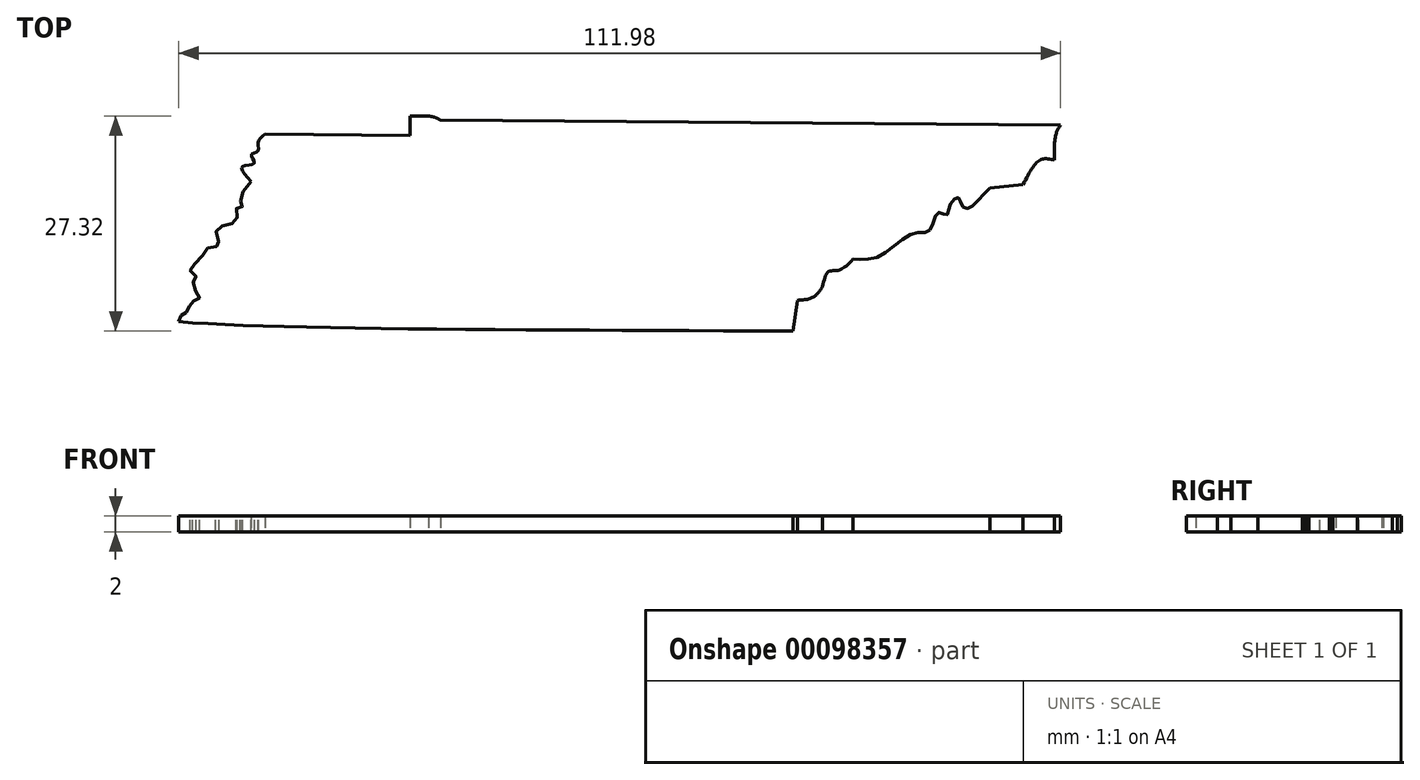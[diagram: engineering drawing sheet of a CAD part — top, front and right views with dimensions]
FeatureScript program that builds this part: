
annotation { "Feature Type Name" : "Feature", "Feature Type Description" : "" }
export const myFeature = defineFeature(function(context is Context, id is Id, definition is map)
    precondition{}
    {
        {
            var Q0;
            Q0=qCreatedBy(makeId("Top.planeOp"),FACE);
            var sketch = newSketch(context, id + "F0", { "sketchPlane" : qUnion([Q0])});
            skLineSegment(sketch, "E0", {"start": v(-26.82, 16.94) * mm, "end": v(51.93, 16.28) * mm});
            skFitSpline(sketch, "E1", {"points": [v(51.93, 16.28) * mm, v(51.35, 15.08) * mm, v(51.16, 11.87) * mm], "startDerivative": vector(-1.7, -2.63) * mm, "endDerivative": vector(0.03, -5.95) * mm});
            skFitSpline(sketch, "E2", {"points": [v(51.16, 11.87) * mm, v(49.38, 11.87) * mm, v(47.2, 8.76) * mm], "startDerivative": vector(-4.52, 1.06) * mm, "endDerivative": vector(-3.45, -6.8) * mm});
            skLineSegment(sketch, "E3", {"start": v(47.2, 8.76) * mm, "end": v(43, 8.31) * mm});
            skLineSegment(sketch, "E4", {"start": v(43, 8.31) * mm, "end": v(40.78, 6.04) * mm});
            skFitSpline(sketch, "E5", {"points": [v(40.78, 6.04) * mm, v(39.58, 5.91) * mm, v(38.96, 7.09) * mm, v(37.87, 6.12) * mm, v(37.5, 4.88) * mm, v(36.39, 5.2) * mm, v(35.38, 2.97) * mm, v(33.23, 2.56) * mm, v(28.92, -0.36) * mm, v(25.6, -0.72) * mm], "startDerivative": vector(-13.2, -13.48) * mm, "endDerivative": vector(-18.35, 0.4) * mm});
            skFitSpline(sketch, "E6", {"points": [v(25.6, -0.72) * mm, v(23.75, -2.13) * mm, v(22.51, -2.31) * mm, v(21.72, -4.21) * mm], "startDerivative": vector(-4.68, -5.49) * mm, "endDerivative": vector(-1.48, -7.24) * mm});
            skFitSpline(sketch, "E7", {"points": [v(21.72, -4.21) * mm, v(20.54, -5.55) * mm, v(18.51, -5.95) * mm], "startDerivative": vector(-2.1, -3.26) * mm, "endDerivative": vector(-4.29, -0.18) * mm});
            skLineSegment(sketch, "E8", {"start": v(18.51, -5.95) * mm, "end": v(17.98, -9.87) * mm});
            skFitSpline(sketch, "E9", {"points": [v(17.98, -9.87) * mm, v(-60.05, -8.68) * mm], "startDerivative": vector(-102.57, 0.48) * mm, "endDerivative": vector(-37.82, 3.1) * mm});
            skFitSpline(sketch, "E10", {"points": [v(-60.05, -8.68) * mm, v(-59.73, -7.88) * mm, v(-59.16, -7.52) * mm, v(-58.58, -6.56) * mm, v(-58.02, -5.94) * mm, v(-57.39, -5.57) * mm, v(-58.3, -3.97) * mm, v(-57.83, -3.01) * mm, v(-58.63, -2.14) * mm, v(-57.35, -0.68) * mm, v(-56.26, 0.73) * mm, v(-54.97, 1.01) * mm, v(-55.35, 2.64) * mm, v(-54.32, 3.53) * mm, v(-52.67, 4.22) * mm, v(-52.68, 5.78) * mm, v(-51.98, 5.95) * mm, v(-52.24, 6.84) * mm, v(-50.84, 9.14) * mm], "startDerivative": vector(5.03, 20.07) * mm, "endDerivative": vector(27.54, 29.96) * mm});
            skFitSpline(sketch, "E11", {"points": [v(-50.84, 9.14) * mm, v(-52, 11.04) * mm, v(-50.47, 11.47) * mm, v(-50.84, 12.52) * mm, v(-50, 12.99) * mm, v(-50, 14.06) * mm, v(-49.08, 15.14) * mm], "startDerivative": vector(-10.59, 11.33) * mm, "endDerivative": vector(7.6, 5.67) * mm});
            skLineSegment(sketch, "E12", {"start": v(-49.08, 15.14) * mm, "end": v(-30.67, 14.96) * mm});
            skLineSegment(sketch, "E13", {"start": v(-30.67, 14.96) * mm, "end": v(-30.67, 17.45) * mm});
            skLineSegment(sketch, "E14", {"start": v(-30.67, 17.45) * mm, "end": v(-28.3, 17.45) * mm});
            skFitSpline(sketch, "E15", {"points": [v(-28.3, 17.45) * mm, v(-27.4, 17.24) * mm, v(-26.82, 16.94) * mm], "startDerivative": vector(1.75, -0.31) * mm, "endDerivative": vector(1.2, -0.71) * mm});
            skSolve(sketch);
        }
        {
            var Q0;
            Q0 = qSketchRegion(id + "F0", true);
            extrude(context, id + "F1", {"entities" : qUnion([Q0]), "depth" : 2 * mm, "offsetDistance" : 25 * mm});
        }
    });
